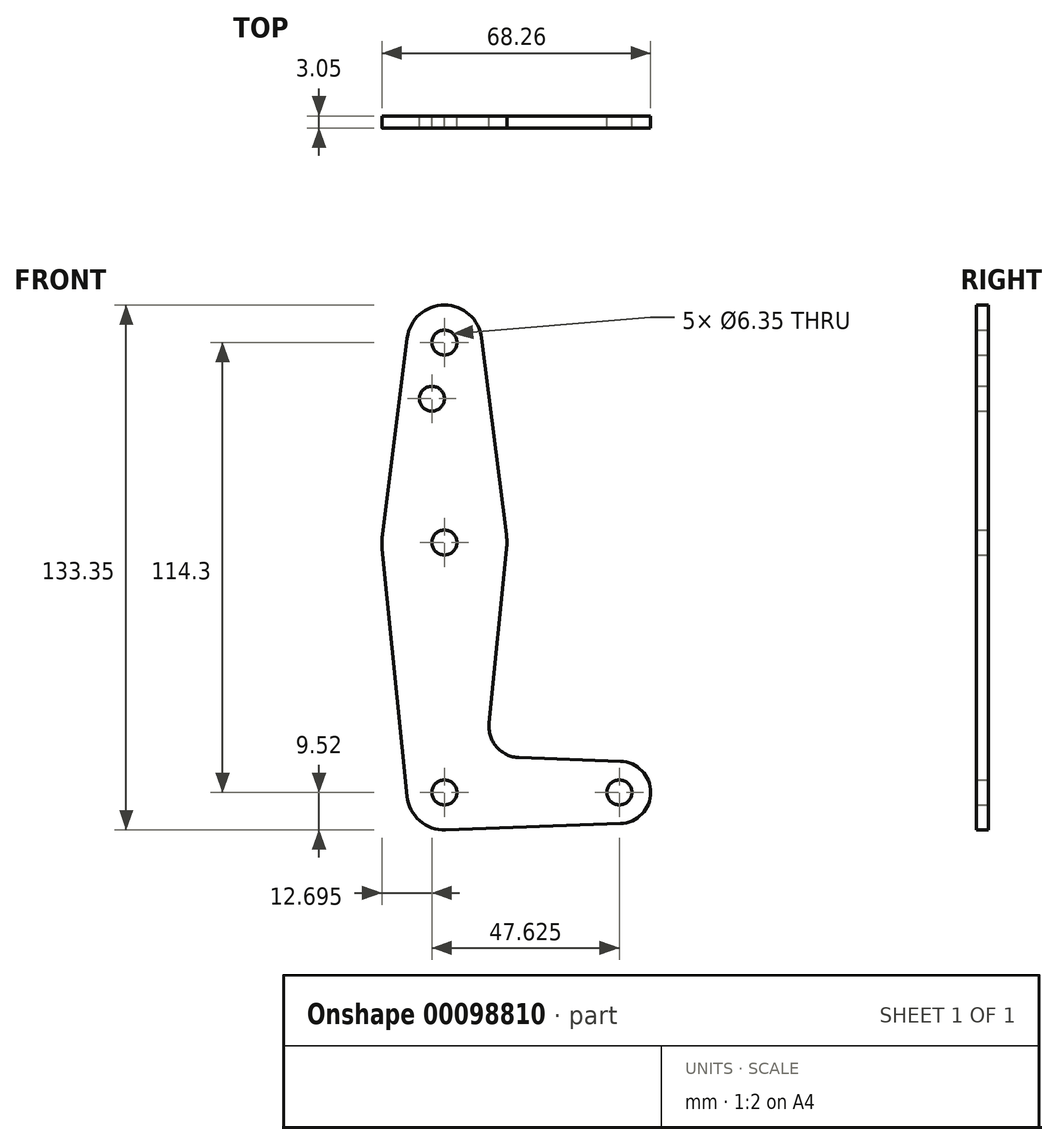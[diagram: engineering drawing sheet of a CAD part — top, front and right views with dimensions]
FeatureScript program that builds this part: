
annotation { "Feature Type Name" : "Feature", "Feature Type Description" : "" }
export const myFeature = defineFeature(function(context is Context, id is Id, definition is map)
    precondition{}
    {
        {
            var Q0;
            Q0=qCreatedBy(makeId("Front.planeOp"),FACE);
            var sketch = newSketch(context, id + "F0", { "sketchPlane" : qUnion([Q0])});
            skLineSegment(sketch, "E0", {"start": v(0, 63.5) * mm, "end": v(0, 0) * mm, "construction": true});
            skLineSegment(sketch, "E1", {"start": v(0, 0) * mm, "end": v(44.45, 0) * mm, "construction": true});
            skLineSegment(sketch, "E2", {"start": v(0, 63.5) * mm, "end": v(0, 114.3) * mm, "construction": true});
            skCircle(sketch, "E3", {"center": v(0, 0) * mm, "radius": 9.53 * mm});
            skCircle(sketch, "E4", {"center": v(44.45, 0) * mm, "radius": 7.94 * mm});
            skCircle(sketch, "E5", {"center": v(0, 63.5) * mm, "radius": 15.88 * mm});
            skLineSegment(sketch, "E6", {"start": v(15.8, 61.91) * mm, "end": v(11.34, 17.6) * mm});
            skLineSegment(sketch, "E7", {"start": v(-15.8, 61.91) * mm, "end": v(-9.48, -0.95) * mm});
            skCircle(sketch, "E8", {"center": v(0, 114.3) * mm, "radius": 9.53 * mm});
            skLineSegment(sketch, "E9", {"start": v(-9.45, 115.5) * mm, "end": v(-15.75, 65.48) * mm});
            skLineSegment(sketch, "E10", {"start": v(0.34, -9.52) * mm, "end": v(44.73, -7.93) * mm});
            skLineSegment(sketch, "E11", {"start": v(15.75, 65.48) * mm, "end": v(9.45, 115.5) * mm});
            skLineSegment(sketch, "E12", {"start": v(18.97, 8.85) * mm, "end": v(44.73, 7.93) * mm});
            skCircle(sketch, "E13", {"center": v(0, 114.3) * mm, "radius": 3.18 * mm});
            skCircle(sketch, "E14", {"center": v(0, 63.5) * mm, "radius": 3.18 * mm});
            skCircle(sketch, "E15", {"center": v(0, 0) * mm, "radius": 3.18 * mm});
            skCircle(sketch, "E16", {"center": v(44.45, 0) * mm, "radius": 3.18 * mm});
            skCircle(sketch, "E17", {"center": v(-3.18, 100.03) * mm, "radius": 3.18 * mm});
            skArc(sketch, "E18.filletArc", {"start": v(11.34, 17.6) * mm, "mid": v(13.26, 11.57) * mm, "end": v(18.97, 8.85) * mm});
            skSolve(sketch);
        }
        {
            var Q0;
            Q0 = qSketchRegion(id + "F0", true);
            extrude(context, id + "F1", {"entities" : qUnion([Q0]), "depth" : 3.05 * mm});
        }
    });
